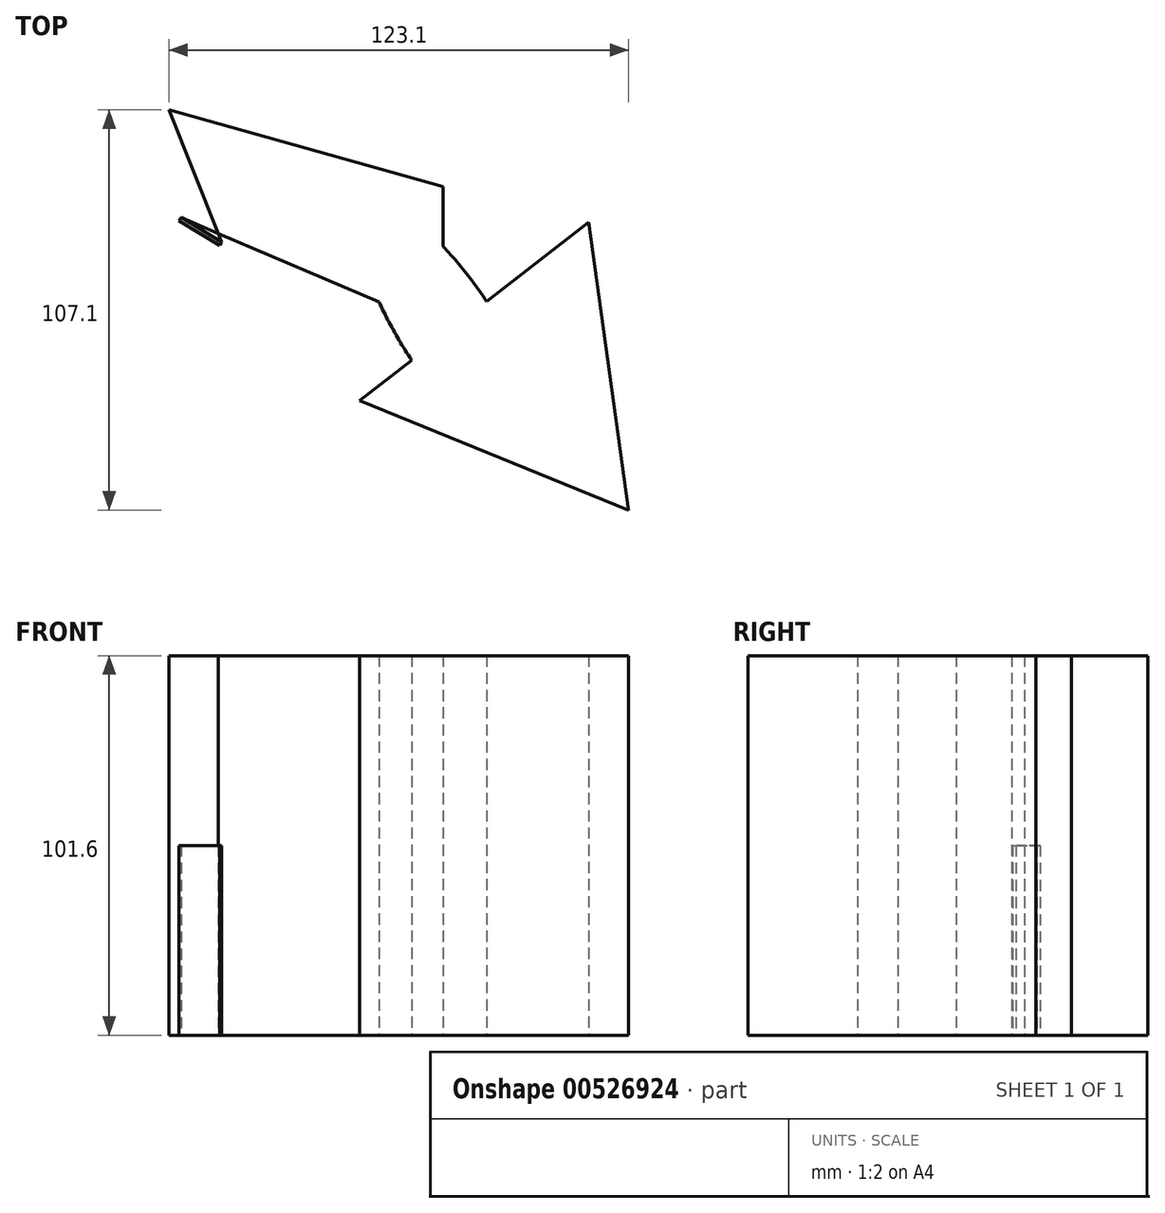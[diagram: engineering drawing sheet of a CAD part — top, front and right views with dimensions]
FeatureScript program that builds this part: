
annotation { "Feature Type Name" : "Feature", "Feature Type Description" : "" }
export const myFeature = defineFeature(function(context is Context, id is Id, definition is map)
    precondition{}
    {
        {
            var Q0;
            Q0=qCreatedBy(makeId("Top.planeOp"),FACE);
            var sketch = newSketch(context, id + "F0", { "sketchPlane" : qUnion([Q0])});
            skLineSegment(sketch, "E0", {"start": v(0, 0) * mm, "end": v(0, 38.1) * mm});
            skLineSegment(sketch, "E1", {"start": v(0, 38.1) * mm, "end": v(-73.37, 58.67) * mm});
            skLineSegment(sketch, "E2", {"start": v(-73.37, 58.67) * mm, "end": v(-59.23, 23.3) * mm});
            skLineSegment(sketch, "E3", {"start": v(-59.23, 23.3) * mm, "end": v(-70.13, 29.81) * mm});
            skLineSegment(sketch, "E4", {"start": v(-70.13, 29.81) * mm, "end": v(0, 0) * mm});
            skEllipse(sketch, "E5", {"center": v(1.36, 0) * mm, "majorRadius": 12.7 * mm, "minorRadius": 38.1 * mm, "majorAxis": v(-0.84, -0.55)});
            skCircle(sketch, "E6.cCircle", {"center": v(22.15, -13.01) * mm, "radius": 22.44 * mm, "construction": true});
            skLineSegment(sketch, "E6.0", {"start": v(39.04, 28.58) * mm, "end": v(49.73, -48.43) * mm});
            skLineSegment(sketch, "E6.1", {"start": v(49.73, -48.43) * mm, "end": v(-22.3, -19.18) * mm});
            skLineSegment(sketch, "E6.2", {"start": v(-22.3, -19.18) * mm, "end": v(39.04, 28.58) * mm});
            skPoint(sketch, "E6.0.midPoint", {"position": v(44.39, -9.93) * mm});
            skSolve(sketch);
        }
        {
            var Q0;
            Q0=qCreatedBy(makeId("Top.planeOp"),FACE);
            var sketch = newSketch(context, id + "F1", { "sketchPlane" : qUnion([Q0])});
            skSolve(sketch);
        }
        {
            var Q0;
            Q0 = qSketchRegion(id + "F0", true);
            extrude(context, id + "F2", {"entities" : qUnion([Q0]), "depth" : 25.4 * mm, "offsetDistance" : 25.4 * mm});
        }
        {
            var Q0;
            Q0 = qSketchRegion(id + "F0", true);
            extrude(context, id + "F3", {"entities" : qUnion([Q0]), "operationType" : NewBodyOperationType.ADD, "depth" : 25.4 * mm, "offsetDistance" : 25.4 * mm});
        }
        {
            var Q0;
            Q0 = qSketchRegion(id + "F0", true);
            extrude(context, id + "F4", {"entities" : qUnion([Q0]), "operationType" : NewBodyOperationType.ADD, "depth" : 25.4 * mm, "offsetDistance" : 25.4 * mm});
        }
        {
            var Q0;
            Q0 = qSketchRegion(id + "F0", true);
            extrude(context, id + "F5", {"entities" : qUnion([Q0]), "operationType" : NewBodyOperationType.ADD, "depth" : 50.8 * mm, "offsetDistance" : 25.4 * mm});
        }
        {
            var Q0;
            Q0 = qSketchRegion(id + "F0", true);
            extrude(context, id + "F6", {"entities" : qUnion([Q0]), "operationType" : NewBodyOperationType.ADD, "depth" : 25.4 * mm, "offsetDistance" : 25.4 * mm});
        }
        {
            var Q0;
            Q0=makeQuery(id+"F5.opExtrude","CAP_FACE",FACE,{"disambiguationData":[OSD([sQuery(id+"F0.wireOp",EDGE,"E0"),sQuery(id+"F0.wireOp",EDGE,"E1"),sQuery(id+"F0.wireOp",EDGE,"E2"),sQuery(id+"F0.wireOp",EDGE,"E3"),sQuery(id+"F0.wireOp",EDGE,"E4"),sQuery(id+"F0.wireOp",EDGE,"E5"),sQuery(id+"F0.wireOp",EDGE,"E6.0"),sQuery(id+"F0.wireOp",EDGE,"E6.1"),sQuery(id+"F0.wireOp",EDGE,"E6.2")])],"isStart":false});
            var Q1;
            Q1 = qSketchRegion(id + "F0", true);
            extrude(context, id + "F7", {"entities" : qUnion([Q0, Q1]), "operationType" : NewBodyOperationType.ADD, "depth" : 25.4 * mm, "offsetDistance" : 25.4 * mm});
        }
        {
            var Q0;
            {var subQ0=sQuery(id+"F0.wireOp",EDGE,"E3");Q0=makeQuery(id+"F5.boolean.opBoolean","MERGE",FACE,{"derivedFrom":[makeQuery(id+"F2.opExtrude","SWEPT_FACE",FACE,{"disambiguationData":[OSD([subQ0])]}),makeQuery(id+"F5.opExtrude","SWEPT_FACE",FACE,{"disambiguationData":[OSD([subQ0])]})]});}
            var Q1;
            Q1 = qSketchRegion(id + "F1", true);
            extrude(context, id + "F8", {"entities" : qUnion([Q0, Q1]), "depth" : 1.02 * mm, "offsetDistance" : 25.4 * mm});
        }
        {
            var Q0;
            {var subQ0=sQuery(id+"F0.wireOp",EDGE,"cTCiTzzW-wzq1-pWts-ctPf-qparT6oLuRsN");var subQ1=sQuery(id+"F0.wireOp",EDGE,"E6.2");var subQ2=sQuery(id+"F0.wireOp",EDGE,"E6.1");var subQ3=sQuery(id+"F0.wireOp",EDGE,"E6.0");var subQ4=sQuery(id+"F0.wireOp",EDGE,"E5");var subQ5=sQuery(id+"F0.wireOp",EDGE,"E4");var subQ6=sQuery(id+"F0.wireOp",EDGE,"E2");var subQ7=sQuery(id+"F0.wireOp",EDGE,"E1");var subQ8=sQuery(id+"F0.wireOp",EDGE,"E0");Q0=makeQuery(id+"F7.opExtrude","CAP_FACE",FACE,{"disambiguationData":[OSD([subQ8,subQ7,subQ6,subQ5,subQ4,subQ3,subQ2,subQ1,subQ0]),TDD([makeQuery(id+"F5.opExtrude","CAP_FACE",FACE,{"disambiguationData":[OSD([subQ8,subQ7,subQ6,subQ5,subQ4,subQ3,subQ2,subQ1,subQ0])],"isStart":false})])],"isStart":false});}
            extrude(context, id + "F9", {"entities" : qUnion([Q0]), "operationType" : NewBodyOperationType.ADD, "depth" : 25.4 * mm, "offsetDistance" : 25.4 * mm});
        }
    });
